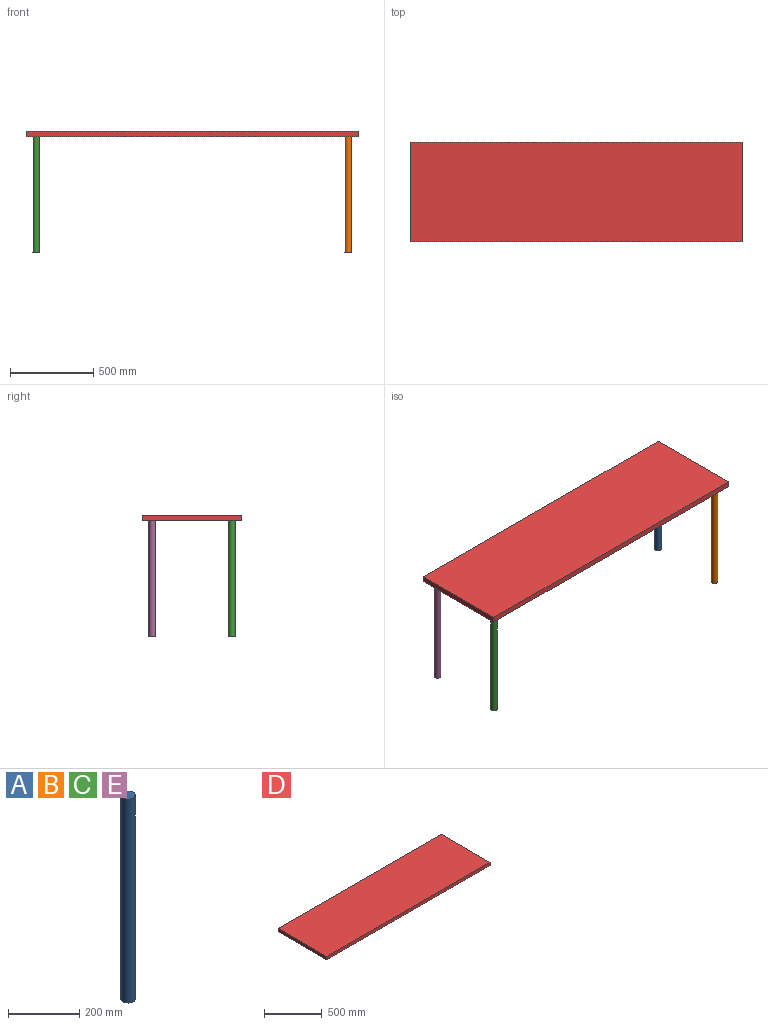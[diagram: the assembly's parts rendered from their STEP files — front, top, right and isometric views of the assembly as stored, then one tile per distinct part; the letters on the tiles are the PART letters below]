
ASSEMBLY  parts=5 mates=4
PART A: 3 faces, bbox 40x40x700 mm
  f0: cylinder r=20mm len=700mm, axis (0,0,1), area 87964.6mm2, adj f1,f2
  f1: plane 40x40mm, normal (0,0,-1), area 1256.6mm2, adj f0
  f2: plane 40x40mm, normal (0,0,1), area 1256.6mm2, adj f0
PART B: same geometry as A
PART C: same geometry as A
PART D: 14 faces, bbox 2000x600x34 mm
  f0: plane 2000x600mm, normal (0,0,-1), area 1199921.5mm2, adj f1,f2,f3,f4,f6,f8,f10,f12
  f1: plane 600x34mm, normal (-1,0,0), area 20400mm2, adj f0,f2,f4,f5
  f2: plane 2000x34mm, normal (0,-1,0), area 68000mm2, adj f0,f1,f3,f5
  f3: plane 600x34mm, normal (1,0,0), area 20400mm2, adj f0,f2,f4,f5
  f4: plane 2000x34mm, normal (0,1,0), area 68000mm2, adj f0,f1,f3,f5
  f5: plane 2000x600mm, normal (0,0,1), area 1200000mm2, adj f1,f2,f3,f4
  f6: cylinder r=2.5mm len=5mm, axis (0,0,-1), area 78.5mm2, adj f0,f7
  f7: plane 5x5mm, normal (0,0,-1), area 19.6mm2, adj f6
  f8: cylinder r=2.5mm len=5mm, axis (0,0,-1), area 78.5mm2, adj f0,f9
  f9: plane 5x5mm, normal (0,0,-1), area 19.6mm2, adj f8
  f10: cylinder r=2.5mm len=5mm, axis (0,0,-1), area 78.5mm2, adj f0,f11
  f11: plane 5x5mm, normal (0,0,-1), area 19.6mm2, adj f10
  f12: cylinder r=2.5mm len=5mm, axis (0,0,-1), area 78.5mm2, adj f0,f13
  f13: plane 5x5mm, normal (0,0,-1), area 19.6mm2, adj f12
PART E: same geometry as A
PLACE A t=(1944.42,617.63,26.01)mm
PLACE B t=(1944.42,137.63,26.01)mm
PLACE C t=(64.42,137.63,26.01)mm
PLACE D t=(4.42,77.63,26.01)mm fixed
PLACE E t=(64.42,617.63,26.01)mm
MATE fastened D.f6 <-> C.f0  axis (0,0,-1) through (64.42,137.63,26.01)mm
MATE fastened B.f0 <-> D.f8  axis (0,0,1) through (1944.42,137.63,26.01)mm
MATE fastened A.f0 <-> D.f10  axis (0,0,1) through (1944.42,617.63,26.01)mm
MATE fastened E.f0 <-> D.f12  axis (0,0,1) through (64.42,617.63,26.01)mm
